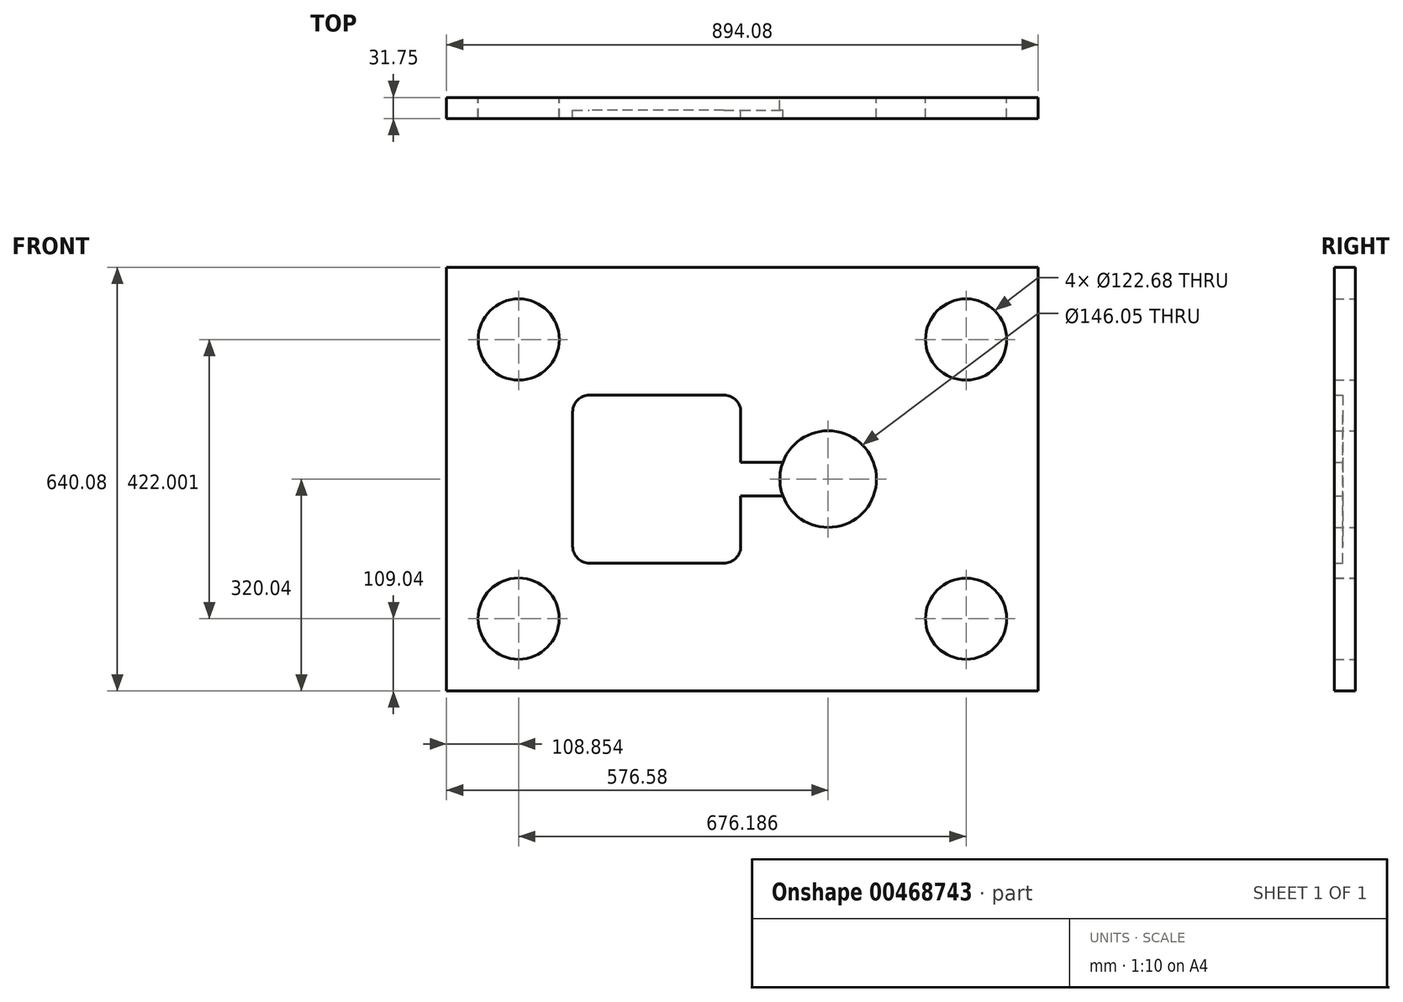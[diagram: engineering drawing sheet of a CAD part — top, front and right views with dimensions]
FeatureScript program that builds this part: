
annotation { "Feature Type Name" : "Feature", "Feature Type Description" : "" }
export const myFeature = defineFeature(function(context is Context, id is Id, definition is map)
    precondition{}
    {
        {
            var Q0;
            Q0=qCreatedBy(makeId("Front.planeOp"),FACE);
            var sketch = newSketch(context, id + "F0", { "sketchPlane" : qUnion([Q0])});
            skLineSegment(sketch, "E0", {"start": v(447.04, -320.04) * mm, "end": v(-447.04, -320.04) * mm});
            skLineSegment(sketch, "E1", {"start": v(-447.04, -320.04) * mm, "end": v(-447.04, 320.04) * mm});
            skCircle(sketch, "E2", {"center": v(-338, 211) * mm, "radius": 61.34 * mm});
            skCircle(sketch, "E3", {"center": v(338, 211) * mm, "radius": 61.34 * mm});
            skCircle(sketch, "E4", {"center": v(338, -211) * mm, "radius": 61.34 * mm});
            skCircle(sketch, "E5", {"center": v(-338.19, -210.81) * mm, "radius": 61.34 * mm});
            skLineSegment(sketch, "E6", {"start": v(-447.04, 320.04) * mm, "end": v(447.04, 320.04) * mm});
            skLineSegment(sketch, "E7", {"start": v(447.04, 320.04) * mm, "end": v(447.04, -320.04) * mm});
            skLineSegment(sketch, "E8", {"start": v(-2.54, 101.6) * mm, "end": v(-2.54, -101.6) * mm});
            skLineSegment(sketch, "E9", {"start": v(-27.94, -127) * mm, "end": v(-231.14, -127) * mm});
            skLineSegment(sketch, "E10", {"start": v(-256.54, -101.6) * mm, "end": v(-256.54, 101.6) * mm});
            skLineSegment(sketch, "E11", {"start": v(-231.14, 127) * mm, "end": v(-27.94, 127) * mm});
            skArc(sketch, "E12", {"start": v(-231.14, 127) * mm, "mid": v(-249.1, 119.56) * mm, "end": v(-256.54, 101.6) * mm});
            skArc(sketch, "E13", {"start": v(-2.54, 101.6) * mm, "mid": v(-9.98, 119.56) * mm, "end": v(-27.94, 127) * mm});
            skArc(sketch, "E14", {"start": v(-27.94, -127) * mm, "mid": v(-9.98, -119.56) * mm, "end": v(-2.54, -101.6) * mm});
            skArc(sketch, "E15", {"start": v(-256.54, -101.6) * mm, "mid": v(-249.1, -119.56) * mm, "end": v(-231.14, -127) * mm});
            skCircle(sketch, "E16", {"center": v(129.54, 0) * mm, "radius": 73.03 * mm});
            skLineSegment(sketch, "E17", {"start": v(-2.54, -25.4) * mm, "end": v(61.07, -25.4) * mm});
            skLineSegment(sketch, "E18", {"start": v(-2.54, 25.4) * mm, "end": v(61.07, 25.4) * mm});
            skSolve(sketch);
        }
        {
            var Q0;
            Q0=makeQuery(id+"F0.imprint","IMPRINT",FACE,{"disambiguationData":[TD([[makeQuery(id+"F0.imprint","IMPRINT",EDGE,{"derivedFrom":sQuery(id+"F0.wireOp",EDGE,"E0")}),-1.0]])]});
            extrude(context, id + "F1", {"entities" : qUnion([Q0]), "depth" : 31.75 * mm});
        }
        {
            var Q0;
            Q0 = qSketchRegion(id + "F0", true);
            var Q1;
            Q1=makeQuery(id+"F0.imprint","IMPRINT",FACE,{"disambiguationData":[TD([[makeQuery(id+"F0.imprint","IMPRINT",EDGE,{"derivedFrom":sQuery(id+"F0.wireOp",EDGE,"E9")}),-1.0]])]});
            extrude(context, id + "F2", {"entities" : qUnion([Q0, Q1]), "operationType" : NewBodyOperationType.ADD, "depth" : 19.05 * mm});
        }
        {
            var Q0;
            {var subQ0=sQuery(id+"F0.wireOp",EDGE,"E17");Q0=makeQuery(id+"F0.imprint","IMPRINT",FACE,{"disambiguationData":[TD([[makeQuery(id+"F0.imprint","IMPRINT",EDGE,{"derivedFrom":subQ0}),1.0]])]});}
            extrude(context, id + "F3", {"entities" : qUnion([Q0]), "operationType" : NewBodyOperationType.ADD, "depth" : 19.05 * mm});
        }
    });
